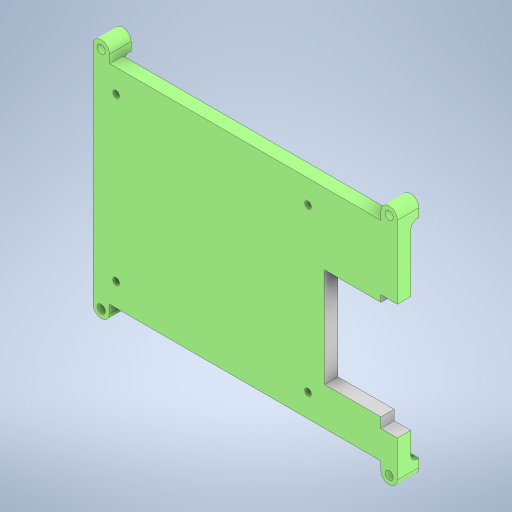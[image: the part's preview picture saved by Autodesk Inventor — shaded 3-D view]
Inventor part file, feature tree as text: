
AUTODESK INVENTOR PART (.ipt)
format: ipt  version: 2023.1 (Build 271208000, 208)  size: 352,768 bytes
history: native  units: mm
features: extrude x4, sketch x3, fillet x2, other x1
ambient origin geometry x8: Origin, YZ Plane, XZ Plane, XY Plane, X Axis, Y Axis, Z Axis, Center Point
bodies: Body1 (feature_tree)
feature tree (10):
  other  "솔리드1"
  sketch  "스케치1"
  extrude  "돌출1"  Depth=92.0mm
  extrude  "돌출3"  Depth=63.0mm
  extrude  "돌출4"  Depth=85.0mm
  fillet  "모깎기1"  Radius=56.0mm
  fillet  "모깎기2"  Radius=3.5mm
  extrude  "돌출5"  Depth=3.5mm
  sketch  "스케치3"
  sketch  "스케치4"
